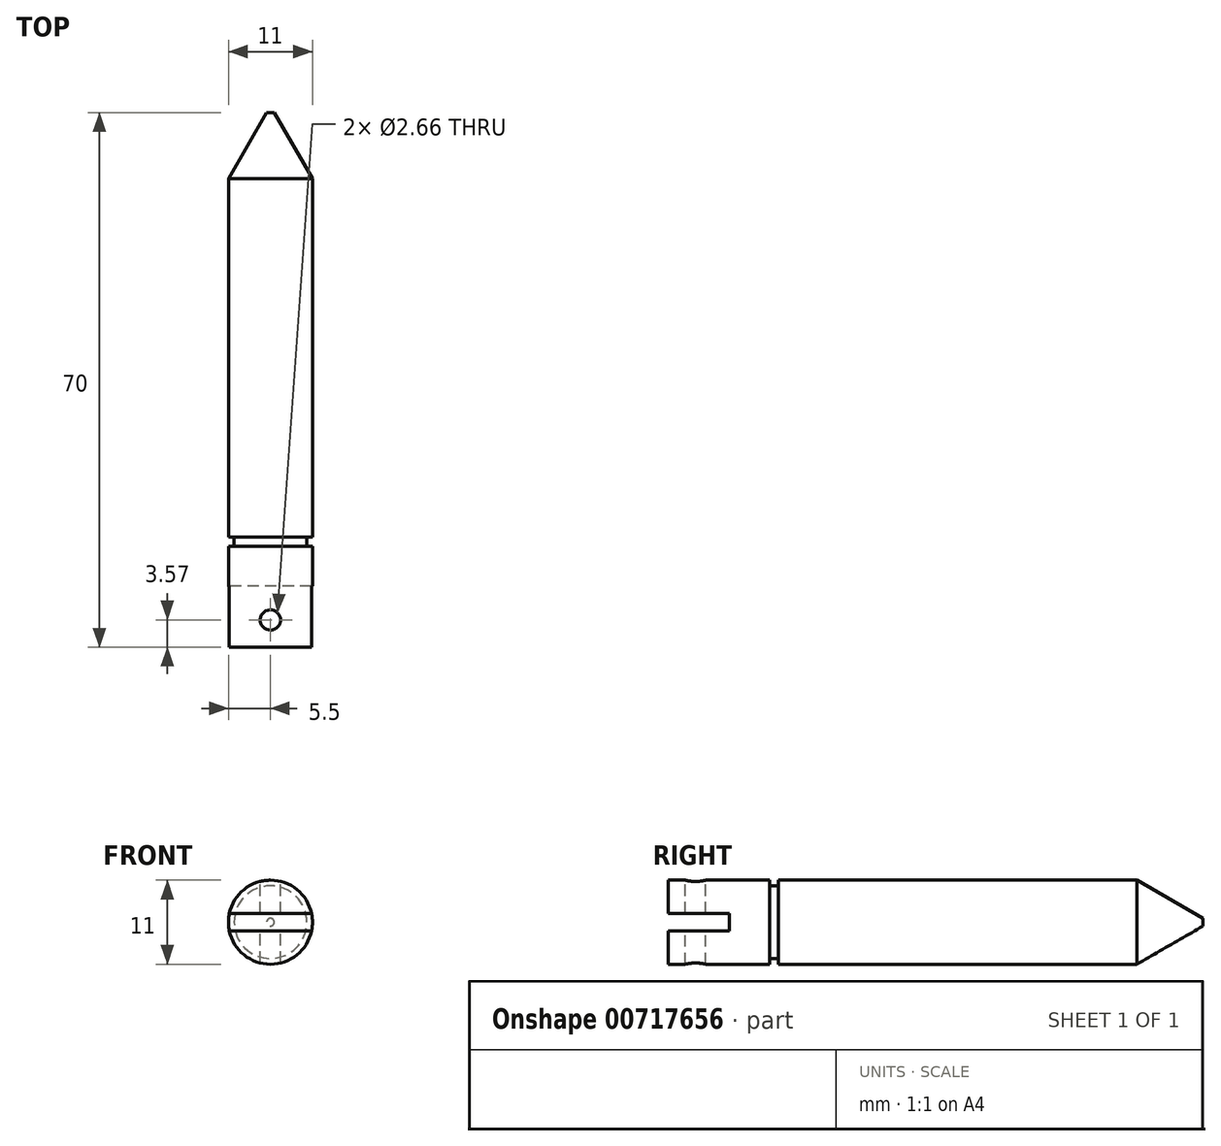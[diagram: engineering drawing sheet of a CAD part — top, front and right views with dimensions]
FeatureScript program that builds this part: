
annotation { "Feature Type Name" : "Feature", "Feature Type Description" : "" }
export const myFeature = defineFeature(function(context is Context, id is Id, definition is map)
    precondition{}
    {
        {
            var Q0;
            Q0=qCreatedBy(makeId("Front.planeOp"),FACE);
            var sketch = newSketch(context, id + "F0", { "sketchPlane" : qUnion([Q0])});
            skCircle(sketch, "E0", {"center": v(0, 0) * mm, "radius": 5.5 * mm});
            skSolve(sketch);
        }
        {
            var Q0;
            Q0 = qSketchRegion(id + "F0", true);
            extrude(context, id + "F1", {"entities" : qUnion([Q0]), "endBound" : BoundingType.SYMMETRIC, "depth" : 70 * mm, "offsetDistance" : 25 * mm});
        }
        {
            var Q0;
            Q0=makeQuery(id+"F1.opExtrude","CAP_EDGE",EDGE,{"disambiguationData":[OSD([sQuery(id+"F0.wireOp",EDGE,"E0")])],"isStart":true});
            chamfer(context, id + "F2", {"entities" : qUnion([Q0]), "chamferType" : ChamferType.OFFSET_ANGLE, "width" : 5 * mm, "oppositeDirection" : true, "angle" : 60 * degree, "tangentPropagation" : true});
        }
        {
            var Q0;
            Q0=makeQuery(id+"F1.opExtrude","CAP_FACE",FACE,{"disambiguationData":[OSD([sQuery(id+"F0.wireOp",EDGE,"E0")])],"isStart":true});
            var sketch = newSketch(context, id + "F3", { "sketchPlane" : qUnion([Q0])});
            skCircle(sketch, "E1.0", {"center": v(0, 0) * mm, "radius": 0.5 * mm});
            skSolve(sketch);
        }
        {
            var Q0;
            Q0=makeQuery(id+"F1.opExtrude","CAP_FACE",FACE,{"disambiguationData":[OSD([sQuery(id+"F0.wireOp",EDGE,"E0")])],"isStart":false});
            var sketch = newSketch(context, id + "F4", { "sketchPlane" : qUnion([Q0])});
            skLineSegment(sketch, "E2.bottom", {"start": v(6.77, -1.14) * mm, "end": v(-6.77, -1.14) * mm});
            skLineSegment(sketch, "E2.top", {"start": v(6.77, 1.14) * mm, "end": v(-6.77, 1.14) * mm});
            skLineSegment(sketch, "E2.left", {"start": v(6.77, -1.14) * mm, "end": v(6.77, 1.14) * mm});
            skLineSegment(sketch, "E2.right", {"start": v(-6.77, -1.14) * mm, "end": v(-6.77, 1.14) * mm});
            skPoint(sketch, "E2.middle", {"position": v(0, 0) * mm});
            skSolve(sketch);
        }
        {
            var Q0;
            Q0 = qSketchRegion(id + "F4", true);
            extrude(context, id + "F5", {"entities" : qUnion([Q0]), "operationType" : NewBodyOperationType.REMOVE, "oppositeDirection" : true, "depth" : 8 * mm, "offsetDistance" : 25 * mm});
        }
        {
            var Q0;
            Q0=qCreatedBy(makeId("Top.planeOp"),FACE);
            var sketch = newSketch(context, id + "F6", { "sketchPlane" : qUnion([Q0])});
            skCircle(sketch, "E3", {"center": v(0, -31.43) * mm, "radius": 1.33 * mm});
            skSolve(sketch);
        }
        {
            var Q0;
            Q0 = qSketchRegion(id + "F6", true);
            extrude(context, id + "F7", {"entities" : qUnion([Q0]), "operationType" : NewBodyOperationType.REMOVE, "endBound" : BoundingType.SYMMETRIC, "oppositeDirection" : true, "depth" : 20 * mm, "offsetDistance" : 25 * mm});
        }
        {
            var Q0;
            Q0=qCreatedBy(makeId("Right.planeOp"),FACE);
            var sketch = newSketch(context, id + "F8", { "sketchPlane" : qUnion([Q0])});
            skLineSegment(sketch, "E4", {"start": v(26.34, -5.5) * mm, "end": v(-35, -5.5) * mm});
            skLineSegment(sketch, "E5", {"start": v(-35, 5.5) * mm, "end": v(26.34, 5.5) * mm});
            skLineSegment(sketch, "E6.bottom", {"start": v(-21.76, 6.96) * mm, "end": v(-20.56, 6.96) * mm});
            skLineSegment(sketch, "E6.top", {"start": v(-21.76, 4.75) * mm, "end": v(-20.56, 4.75) * mm});
            skLineSegment(sketch, "E6.left", {"start": v(-21.76, 6.96) * mm, "end": v(-21.76, 4.75) * mm});
            skLineSegment(sketch, "E6.right", {"start": v(-20.56, 6.96) * mm, "end": v(-20.56, 4.75) * mm});
            skLineSegment(sketch, "E7", {"start": v(-35, 0) * mm, "end": v(0, 0) * mm, "construction": true});
            skSolve(sketch);
        }
        {
            var Q0;
            Q0 = qSketchRegion(id + "F8", true);
            var Q1;
            Q1=sQuery(id+"F8.wireOp",EDGE,"E7");
            revolve(context, id + "F9", {"operationType" : NewBodyOperationType.REMOVE, "surfaceOperationType" : NewSurfaceOperationType.NEW, "entities" : qUnion([Q0]), "axis" : qUnion([Q1]), "revolveType" : RevolveType.FULL, "oppositeDirection" : true});
        }
        {
            var Q0;
            Q0=makeQuery(id+"F1.opExtrude","SWEPT_BODY",BODY,{"disambiguationData":[OSD([sQuery(id+"F0.wireOp",EDGE,"E0")])]});
            transform(context, id + "F10", {"entities" : qUnion([Q0]), "transformType" : TransformType.TRANSLATION_3D, "dx" : 0 * mm, "dy" : 0 * mm, "dz" : 34 * mm, "makeCopy" : true});
        }
        {
            var Q0;
            Q0=makeQuery(id+"F10.opPattern","COPY",BODY,{"derivedFrom":makeQuery(id+"F1.opExtrude","SWEPT_BODY",BODY,{"disambiguationData":[OSD([sQuery(id+"F0.wireOp",EDGE,"E0")])]}),"instanceName":"1"});
            deleteBodies(context, id + "F11", {"entities" : qUnion([Q0])});
        }
        {
            var Q0;
            Q0=makeQuery(id+"F1.opExtrude","SWEPT_BODY",BODY,{"disambiguationData":[OSD([sQuery(id+"F0.wireOp",EDGE,"E0")])]});
            transform(context, id + "F12", {"entities" : qUnion([Q0]), "transformType" : TransformType.TRANSLATION_3D, "dx" : 0 * mm, "dy" : 0 * mm, "dz" : 0 * mm, "makeCopy" : true});
        }
        {
            var Q0;
            Q0=makeQuery(id+"F1.opExtrude","SWEPT_BODY",BODY,{"disambiguationData":[OSD([sQuery(id+"F0.wireOp",EDGE,"E0")])]});
            deleteBodies(context, id + "F13", {"entities" : qUnion([Q0])});
        }
    });
